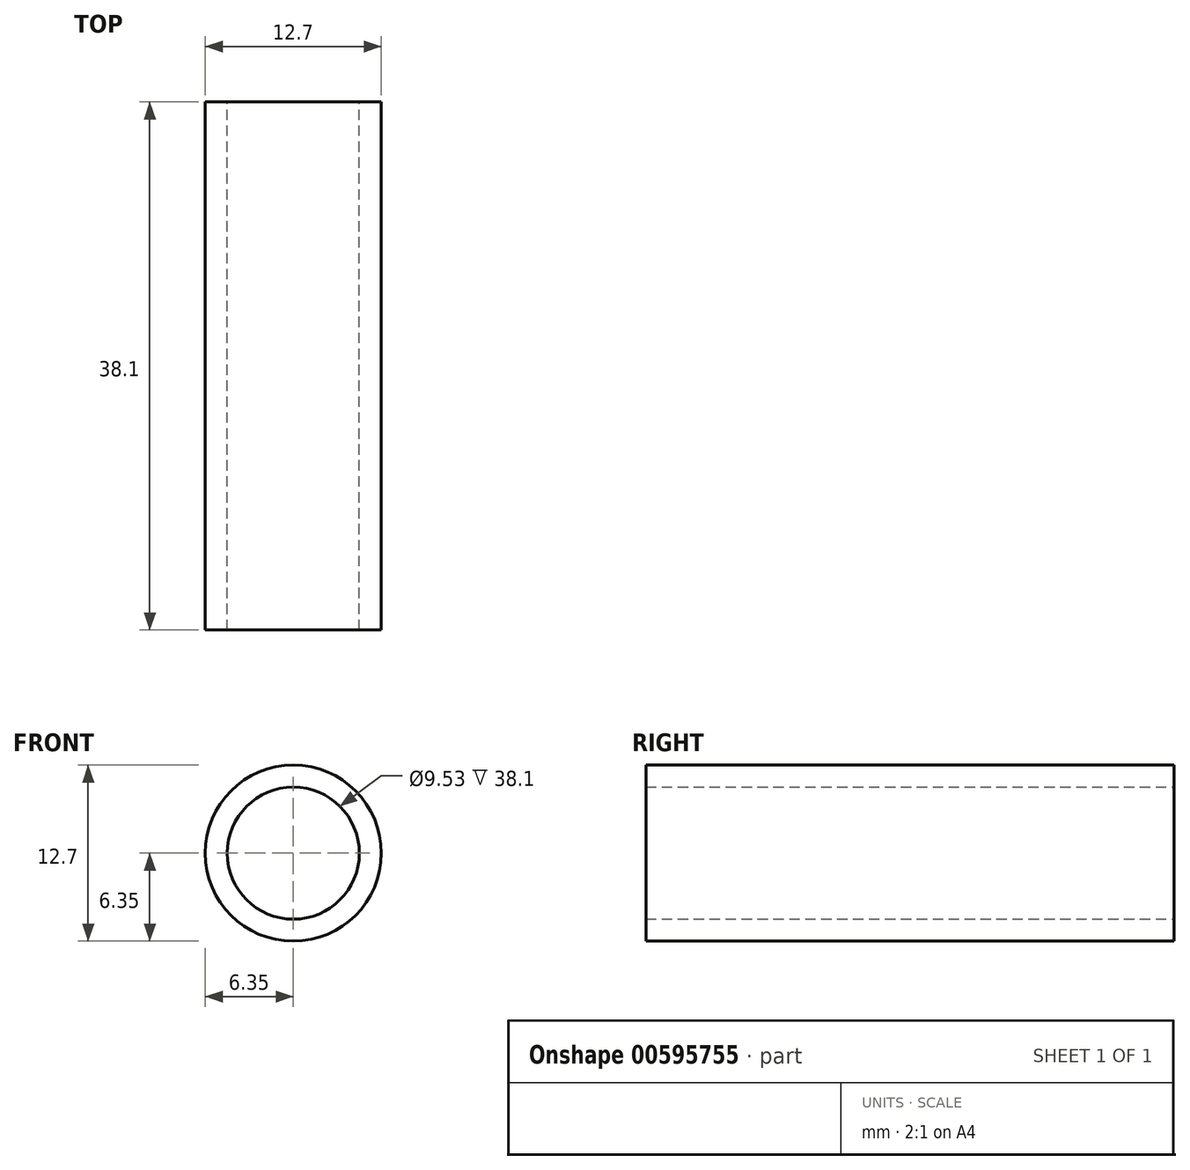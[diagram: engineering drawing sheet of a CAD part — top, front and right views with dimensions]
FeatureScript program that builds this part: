
annotation { "Feature Type Name" : "Feature", "Feature Type Description" : "" }
export const myFeature = defineFeature(function(context is Context, id is Id, definition is map)
    precondition{}
    {
        {
            var Q0;
            Q0=qCreatedBy(makeId("Front.planeOp"),FACE);
            var sketch = newSketch(context, id + "F0", { "sketchPlane" : qUnion([Q0])});
            skCircle(sketch, "E0", {"center": v(0, 0) * mm, "radius": 6.35 * mm});
            skCircle(sketch, "E1", {"center": v(0, 0) * mm, "radius": 4.76 * mm});
            skSolve(sketch);
        }
        {
            var Q0;
            Q0=makeQuery(id+"F0.imprint","IMPRINT",FACE,{"disambiguationData":[TD([[makeQuery(id+"F0.imprint","IMPRINT",EDGE,{"derivedFrom":sQuery(id+"F0.wireOp",EDGE,"E0")}),1.0]])]});
            extrude(context, id + "F1", {"entities" : qUnion([Q0]), "depth" : 38.1 * mm, "offsetDistance" : 25 * mm, "symmetric" : true});
        }
    });
